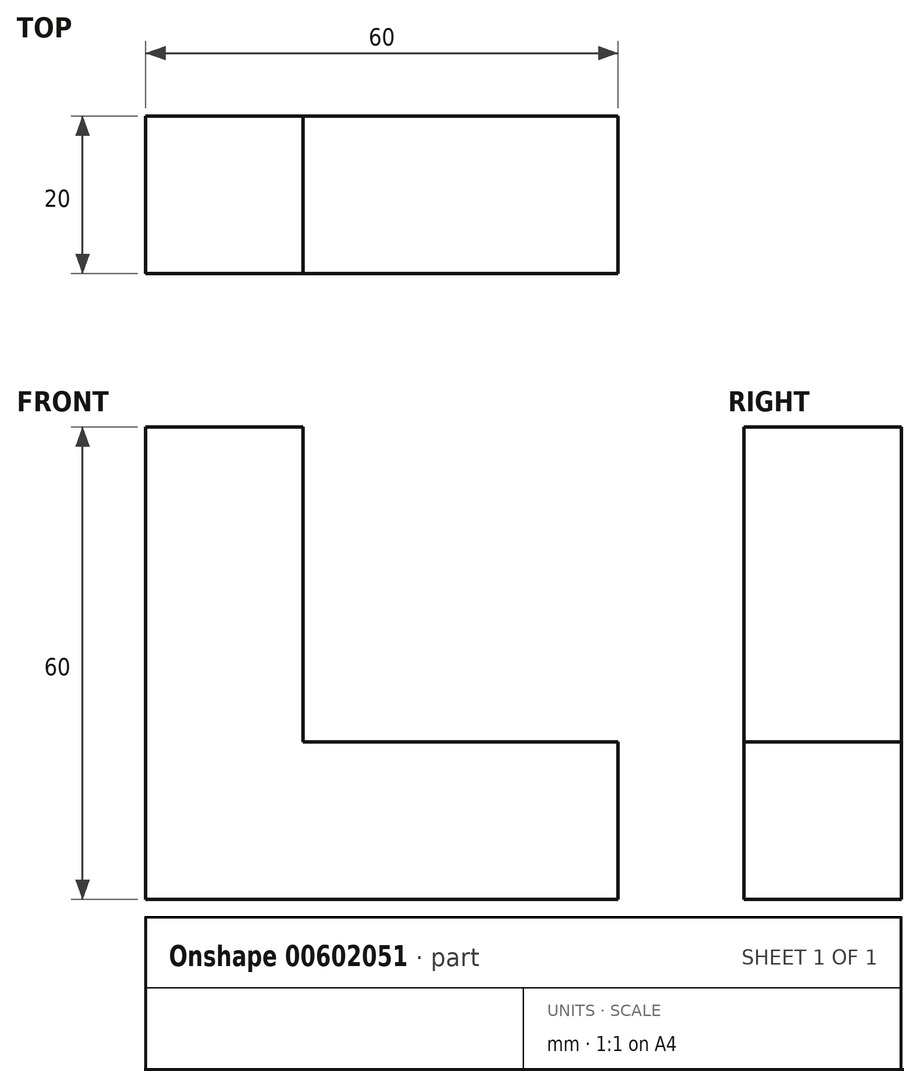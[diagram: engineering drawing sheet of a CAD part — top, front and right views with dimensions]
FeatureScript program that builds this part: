
annotation { "Feature Type Name" : "Feature", "Feature Type Description" : "" }
export const myFeature = defineFeature(function(context is Context, id is Id, definition is map)
    precondition{}
    {
        {
            var Q0;
            Q0=qCreatedBy(makeId("Front.planeOp"),FACE);
            var sketch = newSketch(context, id + "F0", { "sketchPlane" : qUnion([Q0])});
            skLineSegment(sketch, "E0", {"start": v(-60.58, 46.52) * mm, "end": v(-60.58, -13.48) * mm});
            skLineSegment(sketch, "E1", {"start": v(-60.58, -13.48) * mm, "end": v(-0.58, -13.48) * mm});
            skLineSegment(sketch, "E2", {"start": v(-0.58, -13.48) * mm, "end": v(-0.58, 6.52) * mm});
            skLineSegment(sketch, "E3", {"start": v(-0.58, 6.52) * mm, "end": v(-40.58, 6.52) * mm});
            skLineSegment(sketch, "E4", {"start": v(-40.58, 6.52) * mm, "end": v(-40.58, 46.52) * mm});
            skLineSegment(sketch, "E5", {"start": v(-40.58, 46.52) * mm, "end": v(-60.58, 46.52) * mm});
            skSolve(sketch);
        }
        {
            var Q0;
            Q0 = qSketchRegion(id + "F0", true);
            extrude(context, id + "F1", {"entities" : qUnion([Q0]), "depth" : 20 * mm, "offsetDistance" : 25 * mm});
        }
    });
